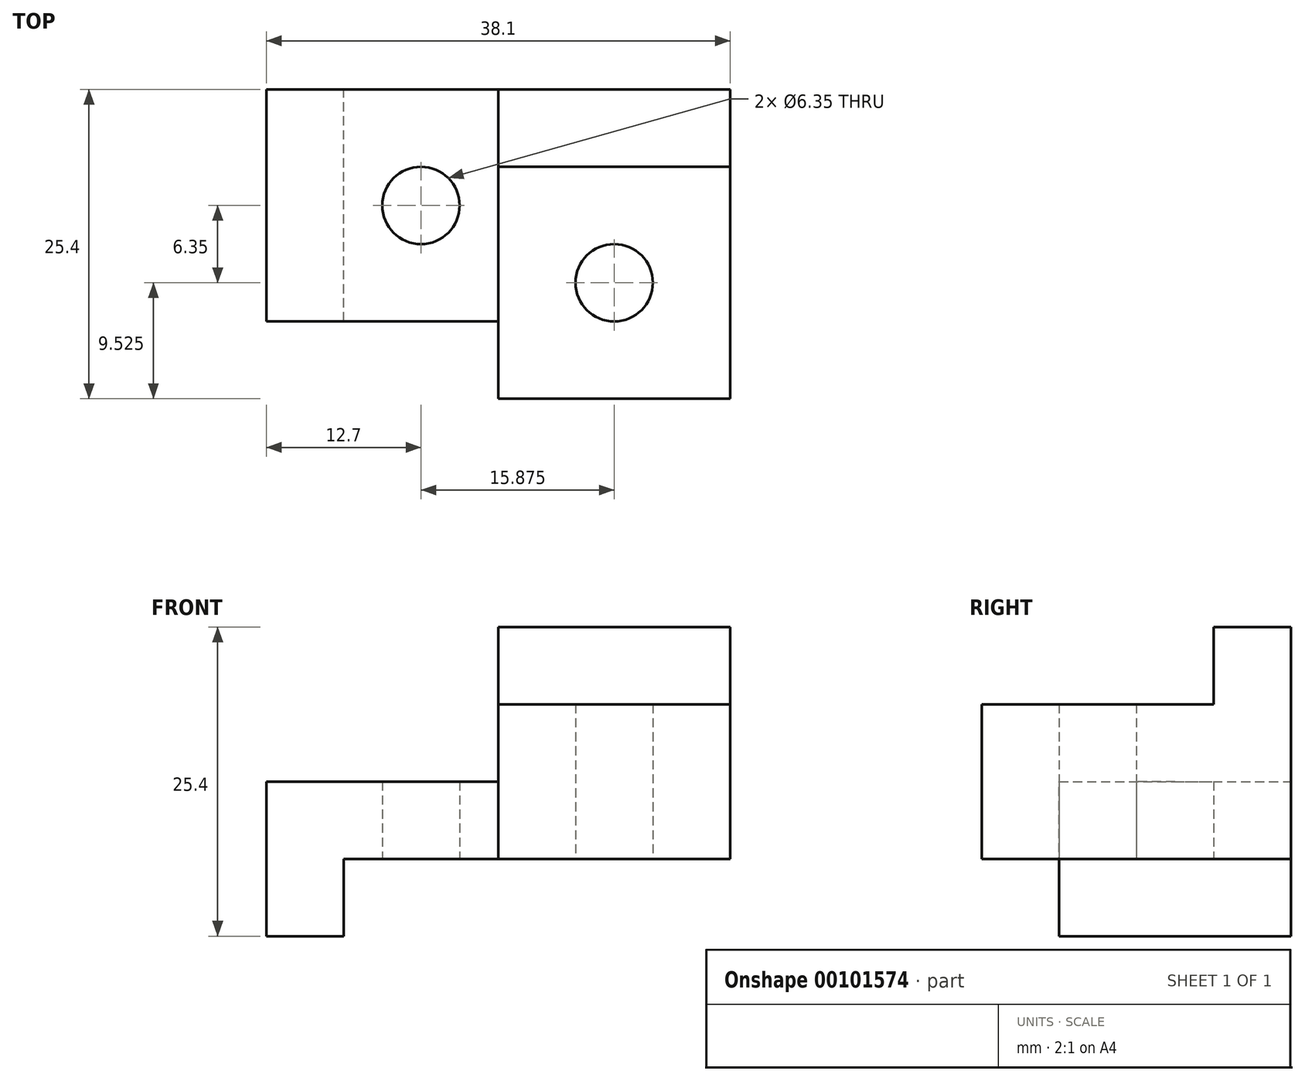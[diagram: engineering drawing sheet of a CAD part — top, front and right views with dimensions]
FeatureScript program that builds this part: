
annotation { "Feature Type Name" : "Feature", "Feature Type Description" : "" }
export const myFeature = defineFeature(function(context is Context, id is Id, definition is map)
    precondition{}
    {
        {
            var Q0;
            Q0=qCreatedBy(makeId("Front.planeOp"),FACE);
            var sketch = newSketch(context, id + "F0", { "sketchPlane" : qUnion([Q0])});
            skLineSegment(sketch, "E0.bottom", {"start": v(0, 0) * mm, "end": v(-19.05, 0) * mm, "construction": true});
            skLineSegment(sketch, "E0.top", {"start": v(0, 12.7) * mm, "end": v(-19.05, 12.7) * mm, "construction": true});
            skLineSegment(sketch, "E0.left", {"start": v(0, 0) * mm, "end": v(0, 12.7) * mm, "construction": true});
            skLineSegment(sketch, "E0.right", {"start": v(-19.05, 0) * mm, "end": v(-19.05, 12.7) * mm, "construction": true});
            skLineSegment(sketch, "E1", {"start": v(-19.05, 0) * mm, "end": v(-19.05, 12.7) * mm});
            skLineSegment(sketch, "E2", {"start": v(0, 12.7) * mm, "end": v(0, 6.35) * mm});
            skLineSegment(sketch, "E3", {"start": v(0, 6.35) * mm, "end": v(-12.7, 6.35) * mm});
            skPoint(sketch, "E3.endSnap0", {"position": v(-19.05, 6.35) * mm});
            skLineSegment(sketch, "E4", {"start": v(-12.7, 6.35) * mm, "end": v(-12.7, 0) * mm});
            skLineSegment(sketch, "E5", {"start": v(-12.7, 0) * mm, "end": v(-19.05, 0) * mm});
            skLineSegment(sketch, "E6", {"start": v(-19.05, 12.7) * mm, "end": v(0, 12.7) * mm});
            skSolve(sketch);
        }
        {
            var Q0;
            Q0=qCreatedBy(makeId("Right.planeOp"),FACE);
            var sketch = newSketch(context, id + "F1", { "sketchPlane" : qUnion([Q0])});
            skLineSegment(sketch, "E7.bottom", {"start": v(0, 0) * mm, "end": v(-25.4, 0) * mm, "construction": true});
            skLineSegment(sketch, "E7.top", {"start": v(0, 25.4) * mm, "end": v(-25.4, 25.4) * mm, "construction": true});
            skLineSegment(sketch, "E7.left", {"start": v(0, 0) * mm, "end": v(0, 25.4) * mm, "construction": true});
            skLineSegment(sketch, "E7.right", {"start": v(-25.4, 0) * mm, "end": v(-25.4, 25.4) * mm, "construction": true});
            skLineSegment(sketch, "E8", {"start": v(0, 6.35) * mm, "end": v(-25.4, 6.35) * mm});
            skLineSegment(sketch, "E9", {"start": v(-25.4, 6.35) * mm, "end": v(-25.4, 19.05) * mm});
            skLineSegment(sketch, "E10", {"start": v(-25.4, 19.05) * mm, "end": v(-6.35, 19.05) * mm});
            skLineSegment(sketch, "E11", {"start": v(-6.35, 19.05) * mm, "end": v(-6.35, 25.4) * mm});
            skLineSegment(sketch, "E12", {"start": v(-6.35, 25.4) * mm, "end": v(0, 25.4) * mm});
            skLineSegment(sketch, "E13", {"start": v(0, 6.35) * mm, "end": v(0, 25.4) * mm});
            skSolve(sketch);
        }
        {
            var Q0;
            Q0 = qSketchRegion(id + "F0", true);
            extrude(context, id + "F2", {"entities" : qUnion([Q0]), "depth" : 19.05 * mm});
        }
        {
            var Q0;
            Q0 = qSketchRegion(id + "F1", true);
            extrude(context, id + "F3", {"entities" : qUnion([Q0]), "operationType" : NewBodyOperationType.ADD, "depth" : 19.05 * mm});
        }
        {
            var Q0;
            Q0=qCreatedBy(makeId("Top.planeOp"),FACE);
            var sketch = newSketch(context, id + "F4", { "sketchPlane" : qUnion([Q0])});
            skCircle(sketch, "E14", {"center": v(-6.35, -9.53) * mm, "radius": 3.18 * mm});
            skCircle(sketch, "E15", {"center": v(9.53, -15.88) * mm, "radius": 3.17 * mm});
            skSolve(sketch);
        }
        {
            var Q0;
            Q0=makeQuery(id+"F4.imprint","IMPRINT",FACE,{"disambiguationData":[TD([[makeQuery(id+"F4.imprint","IMPRINT",EDGE,{"derivedFrom":sQuery(id+"F4.wireOp",EDGE,"E14")}),1.0]])]});
            var Q1;
            Q1=makeQuery(id+"F4.imprint","IMPRINT",FACE,{"disambiguationData":[TD([[makeQuery(id+"F4.imprint","IMPRINT",EDGE,{"derivedFrom":sQuery(id+"F4.wireOp",EDGE,"E15")}),1.0]])]});
            var Q2;
            Q2=sQuery(id+"F4.wireOp",EDGE,"E15");
            var Q3;
            Q3=sQuery(id+"F4.wireOp",EDGE,"E14");
            extrude(context, id + "F5", {"entities" : qUnion([Q0, Q1]), "operationType" : NewBodyOperationType.REMOVE, "surfaceEntities" : qUnion([Q2, Q3]), "endBound" : BoundingType.THROUGH_ALL, "depth" : 25.4 * mm});
        }
    });
